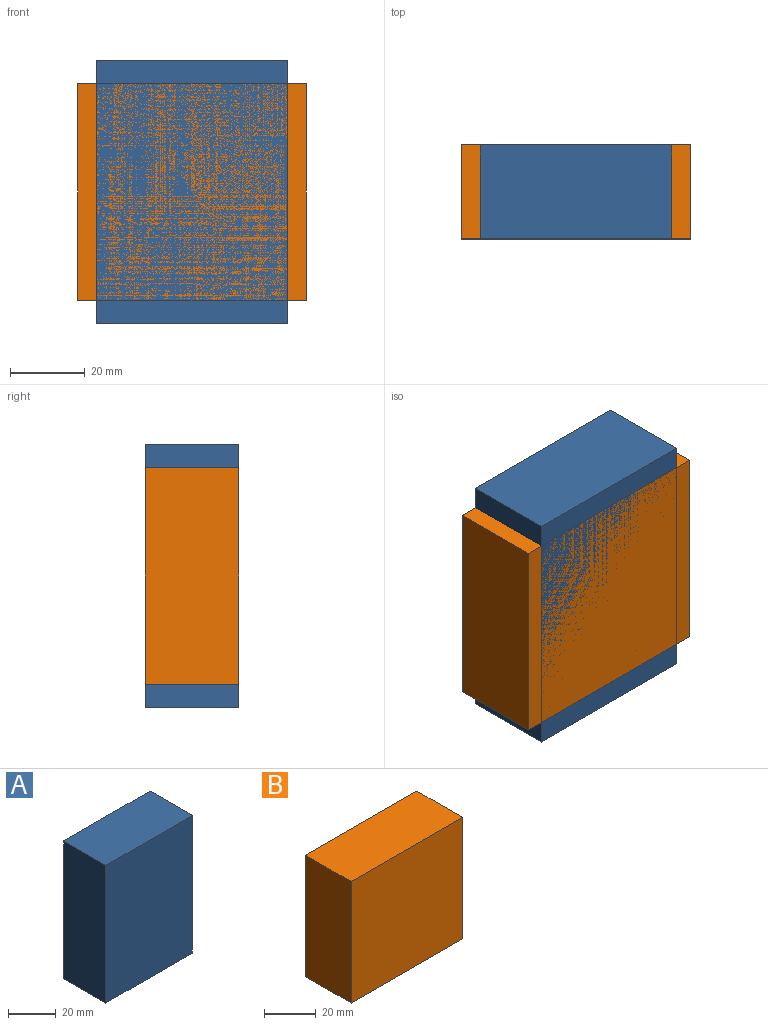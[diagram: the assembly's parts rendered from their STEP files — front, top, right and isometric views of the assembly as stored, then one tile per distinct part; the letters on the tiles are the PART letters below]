
ASSEMBLY  parts=2 mates=1
PART A: 6 faces, bbox 51.2x25x70.4 mm
  f0: plane 51.18x25mm, normal (0,0,1), area 1279.6mm2, adj f1,f3,f4,f5
  f1: plane 70.44x25mm, normal (-1,0,0), area 1761mm2, adj f0,f2,f4,f5
  f2: plane 51.18x25mm, normal (0,0,-1), area 1279.6mm2, adj f1,f3,f4,f5
  f3: plane 70.44x25mm, normal (1,0,0), area 1761mm2, adj f0,f2,f4,f5
  f4: plane 70.44x51.18mm, normal (0,-1,0), area 3605.3mm2, adj f0,f1,f2,f3
  f5: plane 70.44x51.18mm, normal (0,1,0), area 3605.3mm2, adj f0,f1,f2,f3
PART B: 6 faces, bbox 61x25x57.7 mm
  f0: plane 61.02x25mm, normal (0,0,1), area 1525.5mm2, adj f1,f3,f4,f5
  f1: plane 57.66x25mm, normal (-1,0,0), area 1441.5mm2, adj f0,f2,f4,f5
  f2: plane 61.02x25mm, normal (0,0,-1), area 1525.5mm2, adj f1,f3,f4,f5
  f3: plane 57.66x25mm, normal (1,0,0), area 1441.5mm2, adj f0,f2,f4,f5
  f4: plane 61.02x57.66mm, normal (0,-1,0), area 3518.5mm2, adj f0,f1,f2,f3
  f5: plane 61.02x57.66mm, normal (0,1,0), area 3518.5mm2, adj f0,f1,f2,f3
PLACE A at identity
PLACE B t=(92.6,0,-16.16)mm
MATE slider B.f4 <-> A.f4  axis (0,-1,0) through (-25.59,-25,-5.09)mm
